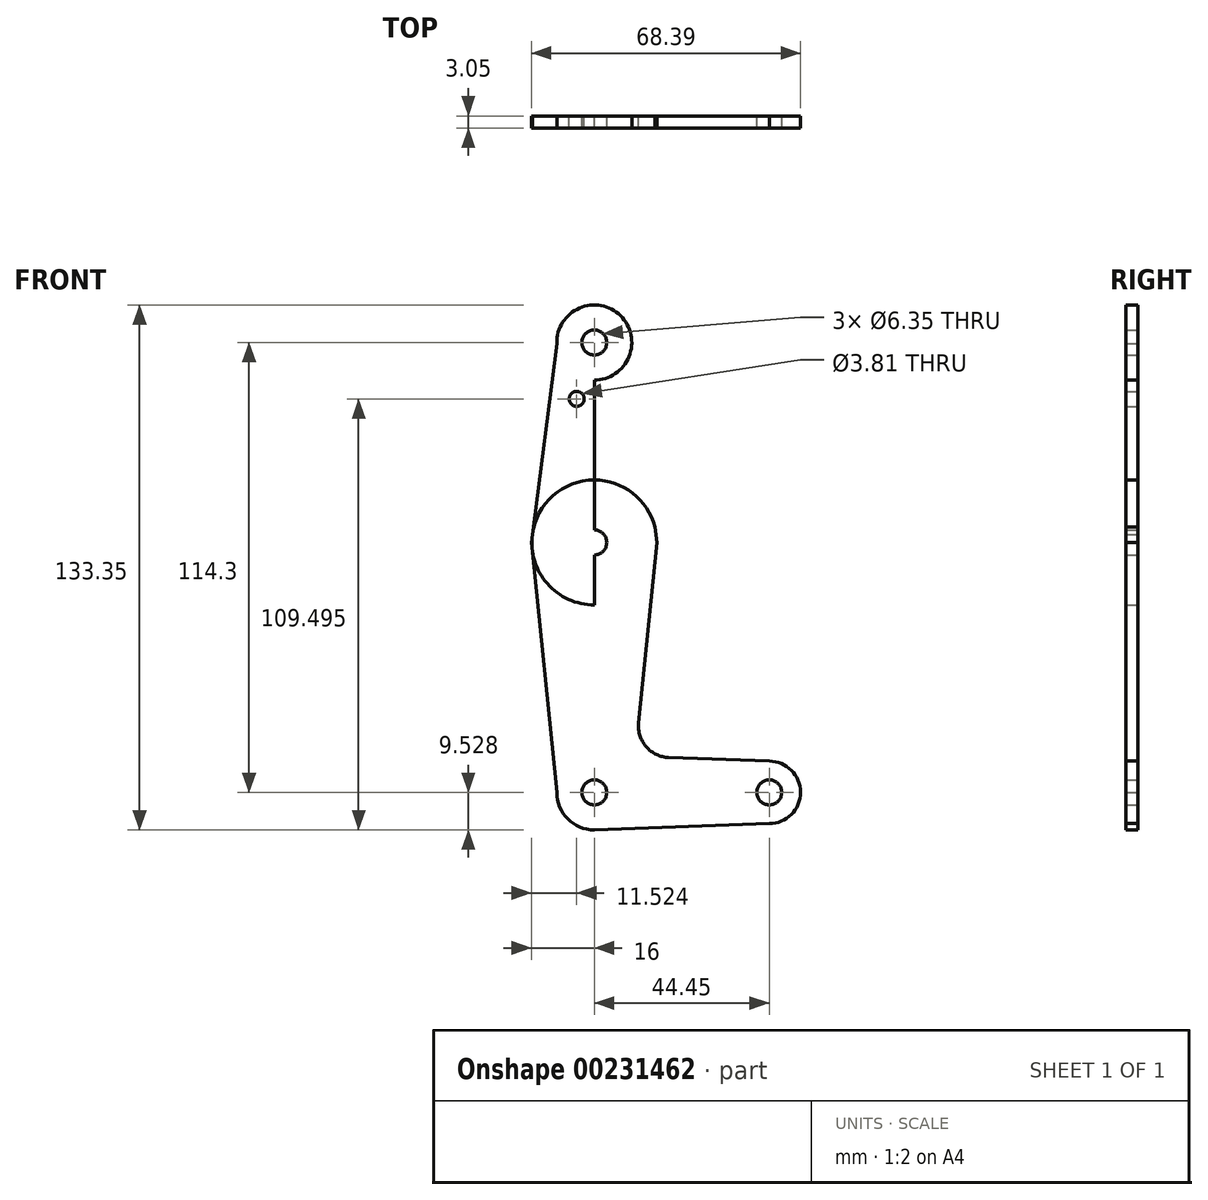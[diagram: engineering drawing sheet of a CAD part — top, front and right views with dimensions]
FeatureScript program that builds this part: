
annotation { "Feature Type Name" : "Feature", "Feature Type Description" : "" }
export const myFeature = defineFeature(function(context is Context, id is Id, definition is map)
    precondition{}
    {
        {
            var Q0;
            Q0=qCreatedBy(makeId("Front.planeOp"),FACE);
            var sketch = newSketch(context, id + "F0", { "sketchPlane" : qUnion([Q0])});
            skLineSegment(sketch, "E0", {"start": v(0, 74.54) * mm, "end": v(0, -39.76) * mm});
            skLineSegment(sketch, "E1", {"start": v(0, -39.76) * mm, "end": v(44.45, -39.76) * mm});
            skCircle(sketch, "E2", {"center": v(0, 74.54) * mm, "radius": 3.18 * mm});
            skCircle(sketch, "E3", {"center": v(44.45, -39.76) * mm, "radius": 3.18 * mm});
            skLineSegment(sketch, "E4", {"start": v(0, -39.76) * mm, "end": v(0, 23.74) * mm});
            skCircle(sketch, "E5", {"center": v(0, 23.74) * mm, "radius": 3.18 * mm});
            skCircle(sketch, "E6", {"center": v(0, -39.76) * mm, "radius": 3.18 * mm});
            skCircle(sketch, "E7", {"center": v(0, 74.54) * mm, "radius": 9.53 * mm});
            skCircle(sketch, "E8", {"center": v(0, 23.74) * mm, "radius": 15.88 * mm});
            skCircle(sketch, "E9", {"center": v(0, -39.76) * mm, "radius": 9.52 * mm});
            skCircle(sketch, "E10", {"center": v(44.45, -39.76) * mm, "radius": 7.94 * mm});
            skLineSegment(sketch, "E11", {"start": v(0, 23.74) * mm, "end": v(0, 60.26) * mm});
            skCircle(sketch, "E12", {"center": v(-4.48, 60.2) * mm, "radius": 1.9 * mm});
            skLineSegment(sketch, "E13", {"start": v(-9.52, 74.33) * mm, "end": v(-16, 23.74) * mm});
            skLineSegment(sketch, "E14", {"start": v(-16, 23.74) * mm, "end": v(-9.52, -39.76) * mm});
            skLineSegment(sketch, "E15", {"start": v(9.52, 74.54) * mm, "end": v(15.88, 23.74) * mm});
            skLineSegment(sketch, "E16", {"start": v(15.88, 23.74) * mm, "end": v(11.28, -22.18) * mm});
            skLineSegment(sketch, "E17", {"start": v(0, -49.29) * mm, "end": v(44.45, -47.7) * mm});
            skLineSegment(sketch, "E18", {"start": v(18.91, -30.91) * mm, "end": v(44.45, -31.82) * mm});
            skArc(sketch, "E19.filletArc", {"start": v(11.28, -22.18) * mm, "mid": v(13.2, -28.2) * mm, "end": v(18.91, -30.91) * mm});
            skSolve(sketch);
        }
        {
            var Q0;
            Q0=makeQuery(id+"F0.imprint","IMPRINT",FACE,{"disambiguationData":[TD([[makeQuery(id+"F0.imprint","IMPRINT",EDGE,{"derivedFrom":sQuery(id+"F0.wireOp",EDGE,"E12")}),-1.0]])]});
            var Q1;
            {var subQ0=sQuery(id+"F0.wireOp",EDGE,"E11");var subQ1=sQuery(id+"F0.wireOp",EDGE,"E0");var subQ2=makeQuery(id+"F0.imprint","INTERSECT",VERTEX,{"derivedFrom":[subQ1,subQ0]});Q1=makeQuery(id+"F0.imprint","IMPRINT",FACE,{"disambiguationData":[TD([[makeQuery(id+"F0.imprint","IMPRINT",EDGE,{"disambiguationData":[TD([[subQ2,1.0]])],"derivedFrom":subQ1}),1.0]])]});}
            var Q2;
            Q2=makeQuery(id+"F0.imprint","IMPRINT",FACE,{"disambiguationData":[TD([[makeQuery(id+"F0.imprint","IMPRINT",EDGE,{"derivedFrom":sQuery(id+"F0.wireOp",EDGE,"E2")}),-1.0]])]});
            var Q3;
            {var subQ1=sQuery(id+"F0.wireOp",EDGE,"E8");var subQ3=sQuery(id+"F0.wireOp",EDGE,"E4");var subQ4=makeQuery(id+"F0.imprint","INTERSECT",VERTEX,{"derivedFrom":[subQ3,subQ1]});Q3=makeQuery(id+"F0.imprint","IMPRINT",FACE,{"disambiguationData":[TD([[makeQuery(id+"F0.imprint","IMPRINT",EDGE,{"disambiguationData":[TD([[subQ4,-1.0]])],"derivedFrom":subQ3}),-1.0]])]});}
            var Q4;
            {var subQ0=sQuery(id+"F0.wireOp",EDGE,"E8");var subQ2=sQuery(id+"F0.wireOp",EDGE,"E4");var subQ3=makeQuery(id+"F0.imprint","INTERSECT",VERTEX,{"derivedFrom":[subQ2,subQ0]});Q4=makeQuery(id+"F0.imprint","IMPRINT",FACE,{"disambiguationData":[TD([[makeQuery(id+"F0.imprint","IMPRINT",EDGE,{"disambiguationData":[TD([[subQ3,-1.0]])],"derivedFrom":subQ2}),1.0]])]});}
            var Q5;
            {var subQ0=sQuery(id+"F0.wireOp",EDGE,"E14");Q5=makeQuery(id+"F0.imprint","IMPRINT",FACE,{"disambiguationData":[TD([[makeQuery(id+"F0.imprint","IMPRINT",EDGE,{"derivedFrom":subQ0}),1.0]])]});}
            var Q6;
            {var subQ5=sQuery(id+"F0.wireOp",EDGE,"E18");Q6=makeQuery(id+"F0.imprint","IMPRINT",FACE,{"disambiguationData":[TD([[makeQuery(id+"F0.imprint","IMPRINT",EDGE,{"derivedFrom":subQ5}),-1.0]])]});}
            var Q7;
            {var subQ0=sQuery(id+"F0.wireOp",EDGE,"E6");var subQ1=sQuery(id+"F0.wireOp",EDGE,"E1");var subQ2=makeQuery(id+"F0.imprint","INTERSECT",VERTEX,{"derivedFrom":[subQ1,subQ0]});Q7=makeQuery(id+"F0.imprint","IMPRINT",FACE,{"disambiguationData":[TD([[makeQuery(id+"F0.imprint","IMPRINT",EDGE,{"disambiguationData":[TD([[subQ2,-1.0]])],"derivedFrom":subQ1}),1.0]])]});}
            var Q8;
            {var subQ4=sQuery(id+"F0.wireOp",EDGE,"E6");var subQ5=sQuery(id+"F0.wireOp",EDGE,"E1");var subQ6=makeQuery(id+"F0.imprint","INTERSECT",VERTEX,{"derivedFrom":[subQ5,subQ4]});Q8=makeQuery(id+"F0.imprint","IMPRINT",FACE,{"disambiguationData":[TD([[makeQuery(id+"F0.imprint","IMPRINT",EDGE,{"disambiguationData":[TD([[subQ6,-1.0]])],"derivedFrom":subQ5}),-1.0]])]});}
            var Q9;
            {var subQ0=sQuery(id+"F0.wireOp",EDGE,"E10");var subQ1=sQuery(id+"F0.wireOp",EDGE,"E1");var subQ2=makeQuery(id+"F0.imprint","INTERSECT",VERTEX,{"derivedFrom":[subQ1,subQ0]});Q9=makeQuery(id+"F0.imprint","IMPRINT",FACE,{"disambiguationData":[TD([[makeQuery(id+"F0.imprint","IMPRINT",EDGE,{"disambiguationData":[TD([[subQ2,1.0]])],"derivedFrom":subQ1}),-1.0]])]});}
            var Q10;
            Q10=makeQuery(id+"F0.imprint","IMPRINT",FACE,{"disambiguationData":[TD([[makeQuery(id+"F0.imprint","IMPRINT",EDGE,{"derivedFrom":sQuery(id+"F0.wireOp",EDGE,"E3")}),-1.0]])]});
            extrude(context, id + "F1", {"entities" : qUnion([Q0, Q1, Q2, Q3, Q4, Q5, Q6, Q7, Q8, Q9, Q10]), "depth" : 3.05 * mm});
        }
    });
